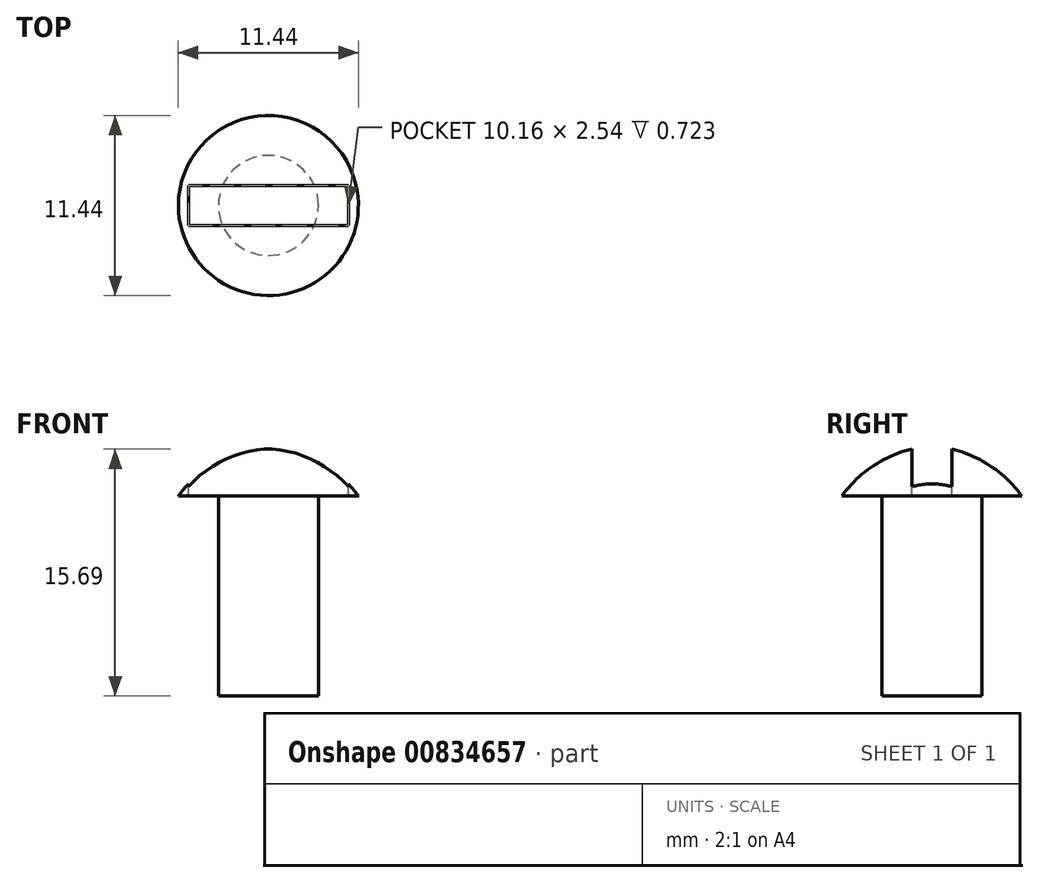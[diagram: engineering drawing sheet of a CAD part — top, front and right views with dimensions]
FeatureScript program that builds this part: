
annotation { "Feature Type Name" : "Feature", "Feature Type Description" : "" }
export const myFeature = defineFeature(function(context is Context, id is Id, definition is map)
    precondition{}
    {
        {
            var Q0;
            Q0=qCreatedBy(makeId("Front.planeOp"),FACE);
            var sketch = newSketch(context, id + "F0", { "sketchPlane" : qUnion([Q0])});
            skLineSegment(sketch, "E0", {"start": v(0, 0) * mm, "end": v(0, 15.88) * mm});
            skLineSegment(sketch, "E1", {"start": v(0, 0) * mm, "end": v(3.17, 0) * mm});
            skLineSegment(sketch, "E2", {"start": v(3.17, 0) * mm, "end": v(3.17, 12.7) * mm});
            skLineSegment(sketch, "E3", {"start": v(3.18, 12.7) * mm, "end": v(5.72, 12.7) * mm});
            skArc(sketch, "E4", {"start": v(5.71, 12.7) * mm, "mid": v(3.22, 14.93) * mm, "end": v(0, 15.88) * mm});
            skLineSegment(sketch, "E5", {"start": v(0, 0) * mm, "end": v(0, 15.88) * mm, "construction": true});
            skSolve(sketch);
        }
        {
            var Q0;
            Q0=makeQuery(id+"F0.imprint","IMPRINT",FACE,{"disambiguationData":[TD([[makeQuery(id+"F0.imprint","IMPRINT",EDGE,{"derivedFrom":sQuery(id+"F0.wireOp",EDGE,"E0")}),-1.0]])]});
            var Q1;
            Q1=sQuery(id+"F0.wireOp",EDGE,"E0");
            revolve(context, id + "F1", {"surfaceOperationType" : NewSurfaceOperationType.NEW, "entities" : qUnion([Q0]), "axis" : qUnion([Q1]), "revolveType" : RevolveType.FULL});
        }
        {
            var Q0;
            Q0=qCreatedBy(makeId("Top.planeOp"),FACE);
            cPlane(context, id + "F2", {"entities" : qUnion([Q0]), "cplaneType" : CPlaneType.OFFSET, "offset" : 15.88 * mm, "width" : 152.4 * mm, "height" : 152.4 * mm});
        }
        {
            var Q0;
            Q0=qCreatedBy(id+"F2.planeOp",FACE);
            var sketch = newSketch(context, id + "F3", { "sketchPlane" : qUnion([Q0])});
            skLineSegment(sketch, "E6.bottom", {"start": v(-5.08, 1.27) * mm, "end": v(5.08, 1.27) * mm});
            skLineSegment(sketch, "E6.top", {"start": v(-5.08, -1.27) * mm, "end": v(5.08, -1.27) * mm});
            skLineSegment(sketch, "E6.left", {"start": v(-5.08, 1.27) * mm, "end": v(-5.08, -1.27) * mm});
            skLineSegment(sketch, "E6.right", {"start": v(5.08, 1.27) * mm, "end": v(5.08, -1.27) * mm});
            skSolve(sketch);
        }
        {
            var Q0;
            Q0=makeQuery(id+"F3.imprint","IMPRINT",FACE,{"disambiguationData":[TD([[makeQuery(id+"F3.imprint","IMPRINT",EDGE,{"derivedFrom":sQuery(id+"F3.wireOp",EDGE,"E6.bottom")}),-1.0]])]});
            extrude(context, id + "F4", {"entities" : qUnion([Q0]), "operationType" : NewBodyOperationType.REMOVE, "oppositeDirection" : true, "depth" : 3.12 * mm, "offsetDistance" : 25.4 * mm});
        }
    });
